# Revit family: LAMP_KOMBIC 100 SURFACE SUSPENDED TRACK OPAL TW
name_source: partatom
category: Luminarias
revit_build: Autodesk Revit 2018 (Build: 20190510_1515(x64)
units: mm (PartAtom-declared; Revit-internal decimal feet)

## family parameters
Anfitrión = Cara
Compartido = No
Corte con vacíos al cargar = No
Cota de conector redondo = Diámetro de uso
Origen de luz = Sí
Punto de cálculo de habitación = No
Tipo de pieza = Normal

## types (6) — shared parameters
CRI = 90
Cambio de temperatura de color de luz atenuada = <Ninguno>
Diameter = 100 mm  [stored 0.328084 ft]
Elevación por defecto = 1219 mm
Fabricante = LAMP
Filtro de color = 16777215
Gear = Electronic
Height = 220 mm  [stored 0.721785 ft]
IEE = A
Initial color = 2700-5000K
Installation instructions = https://www.lamp.es
Insulation class = I
LED Lifetime = 70.000 L80 B10
Lamp = COB LED
Last update = 29/07/2021
Luminaire type = Suspended Track
MacAdam = 3
Manufacturer URL = http://www.lamp.es
Manufacturer country = Spain
Manufacturer name = LAMP
Material cable suspension = LAMP_Acero genérico
Material difusor = LAMP_PMMA Difusor Kombic
Material floron = LAMP_Plástico genérico NG
Model explanation = Possibility to modify the lenght of the suspension cable up to 1m
Power = 16 W
Power Supply = 220-240V 50/60Hz
Product URL = https://www.lamp.es
Product datasheet = http://www.lamp.es
Protection rating = IP40
Type = COB BRIDGELUX
Weight = 0.50 kg
Ángulo de inclinación = -90.00°

## per-type parameters (varying)
| type | Archivo de red fotométrica | Efficacy | Finish | Material cuerpo | Material reflector | Modelo | Plum | Product code |
| 1246LM TWK DALI W/B | K11rd2040OP9TWDWw.IES | 64 lm/W | Matte black RAL 9011 | LAMP_Plástico genérico NG | LAMP_PC Reflector Kombic Blanco | K11ST2040OP9TWDWB | 21 W | K11ST2040OP9TWDWB |
| 1246LM TWK DALI W/W | K11rd2040OP9TWDWW.IES | 64 lm/W | Matte Traffic white RAL 9016 | LAMP_Plástico genérico BL | LAMP_PC Reflector Kombic Blanco | K11ST2040OP9TWDWW | 20 W | K11ST2040OP9TWDWW |
| 1263LM TWK DALI M/B | K11rd2040OP9TWDMw.IES | 65 lm/W | Matte black RAL 9011 | LAMP_Plástico genérico NG | LAMP_PC Reflector Kombic Metalizado Mate | K11ST2040OP9TWDMB | 21 W | K11ST2040OP9TWDMB |
| 1263LM TWK DALI M/W | K11rd2040OP9TWDMW.IES | 65 lm/W | Matte Traffic white RAL 9016 | LAMP_Plástico genérico BL | LAMP_PC Reflector Kombic Metalizado Mate | K11ST2040OP9TWDMW | 21 W | K11ST2040OP9TWDMW |
| 1349LM TWK DALI BR/B | K11rd2040OP9TWDRw.IES | 69 lm/W | Matte black RAL 9011 | LAMP_Plástico genérico NG | LAMP_PC Reflector Kombic Metalizado Brillante | K11ST2040OP9TWDRB | 20 W | K11ST2040OP9TWDRB |
| 1349LM TWK DALI BR/W | K11rd2040OP9TWDRW.IES | 69 lm/W | Matte Traffic white RAL 9016 | LAMP_Plástico genérico BL | LAMP_PC Reflector Kombic Metalizado Brillante | K11ST2040OP9TWDRW | 21 W | K11ST2040OP9TWDRW |

note: [stored X ft] marks values corroborated as IEEE doubles in the binary element streams (Revit-internal decimal feet)
